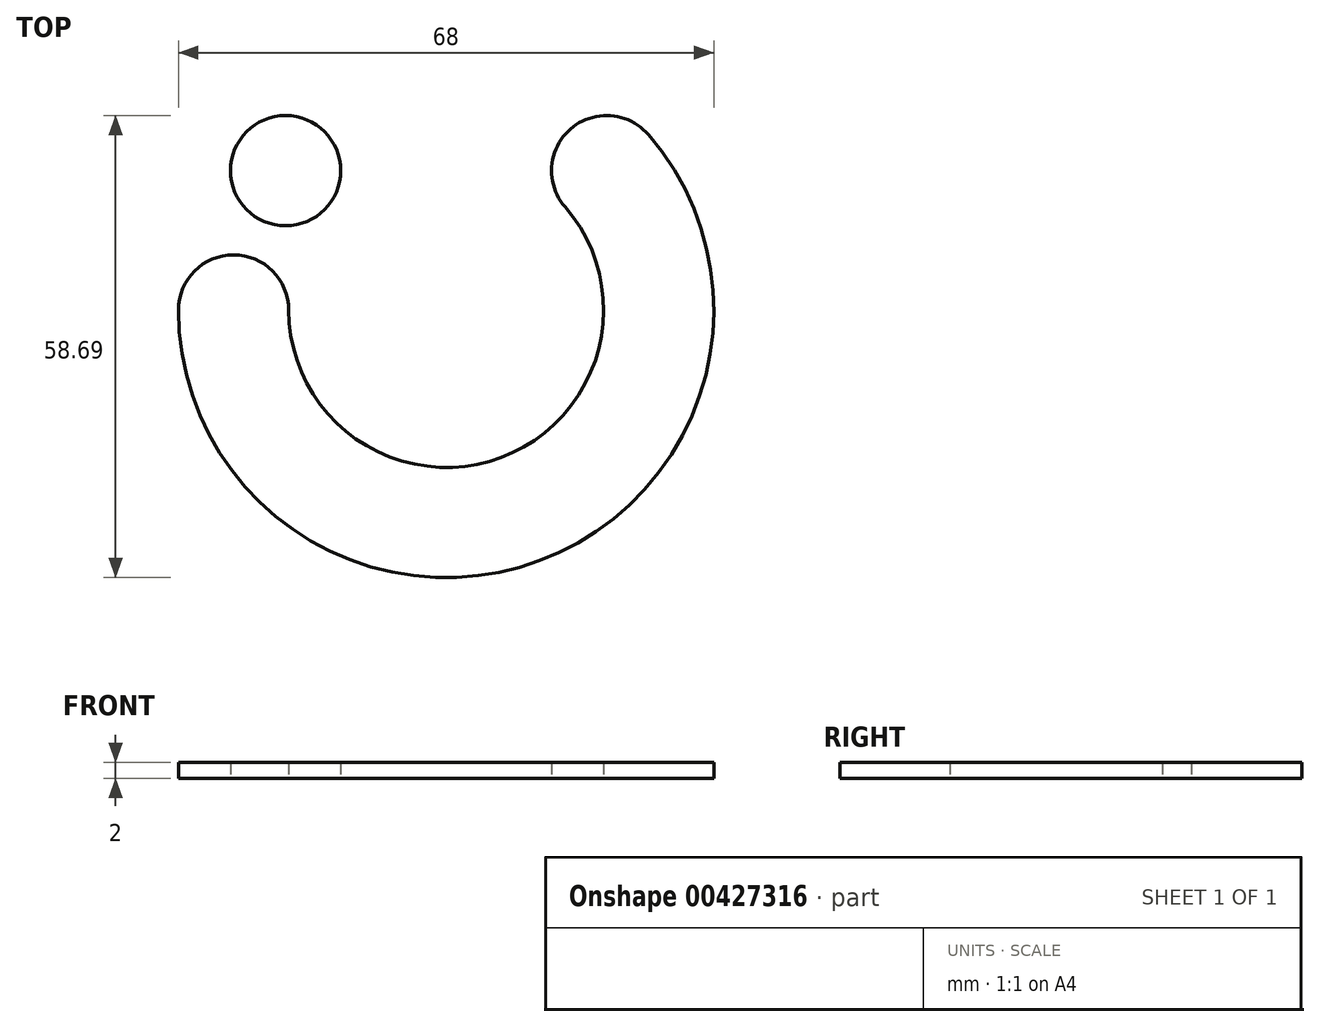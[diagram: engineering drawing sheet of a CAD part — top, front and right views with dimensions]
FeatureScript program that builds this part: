
annotation { "Feature Type Name" : "Feature", "Feature Type Description" : "" }
export const myFeature = defineFeature(function(context is Context, id is Id, definition is map)
    precondition{}
    {
        {
            var Q0;
            Q0=qCreatedBy(makeId("Top.planeOp"),FACE);
            var sketch = newSketch(context, id + "F0", { "sketchPlane" : qUnion([Q0])});
            skArc(sketch, "E0", {"start": v(-34, 0) * mm, "mid": v(11.9, -31.85) * mm, "end": v(25.68, 22.28) * mm});
            skArc(sketch, "E1", {"start": v(-20, 0) * mm, "mid": v(7, -18.74) * mm, "end": v(15.1, 13.1) * mm});
            skArc(sketch, "E2", {"start": v(-20, 0) * mm, "mid": v(-27, 7) * mm, "end": v(-34, 0) * mm});
            skCircle(sketch, "E3", {"center": v(-20.4, 17.7) * mm, "radius": 7 * mm});
            skArc(sketch, "E4.MirrorC", {"start": v(15.1, 13.1) * mm, "mid": v(15.8, 22.98) * mm, "end": v(25.68, 22.28) * mm});
            skSolve(sketch);
        }
        {
            var Q0;
            Q0=makeQuery(id+"F0.imprint","IMPRINT",FACE,{"disambiguationData":[TD([[makeQuery(id+"F0.imprint","IMPRINT",EDGE,{"derivedFrom":sQuery(id+"F0.wireOp",EDGE,"E0")}),1.0]])]});
            var Q1;
            Q1=makeQuery(id+"F0.imprint","IMPRINT",FACE,{"disambiguationData":[TD([[makeQuery(id+"F0.imprint","IMPRINT",EDGE,{"derivedFrom":sQuery(id+"F0.wireOp",EDGE,"E3")}),1.0]])]});
            extrude(context, id + "F1", {"entities" : qUnion([Q0, Q1]), "depth" : 2 * mm});
        }
    });
